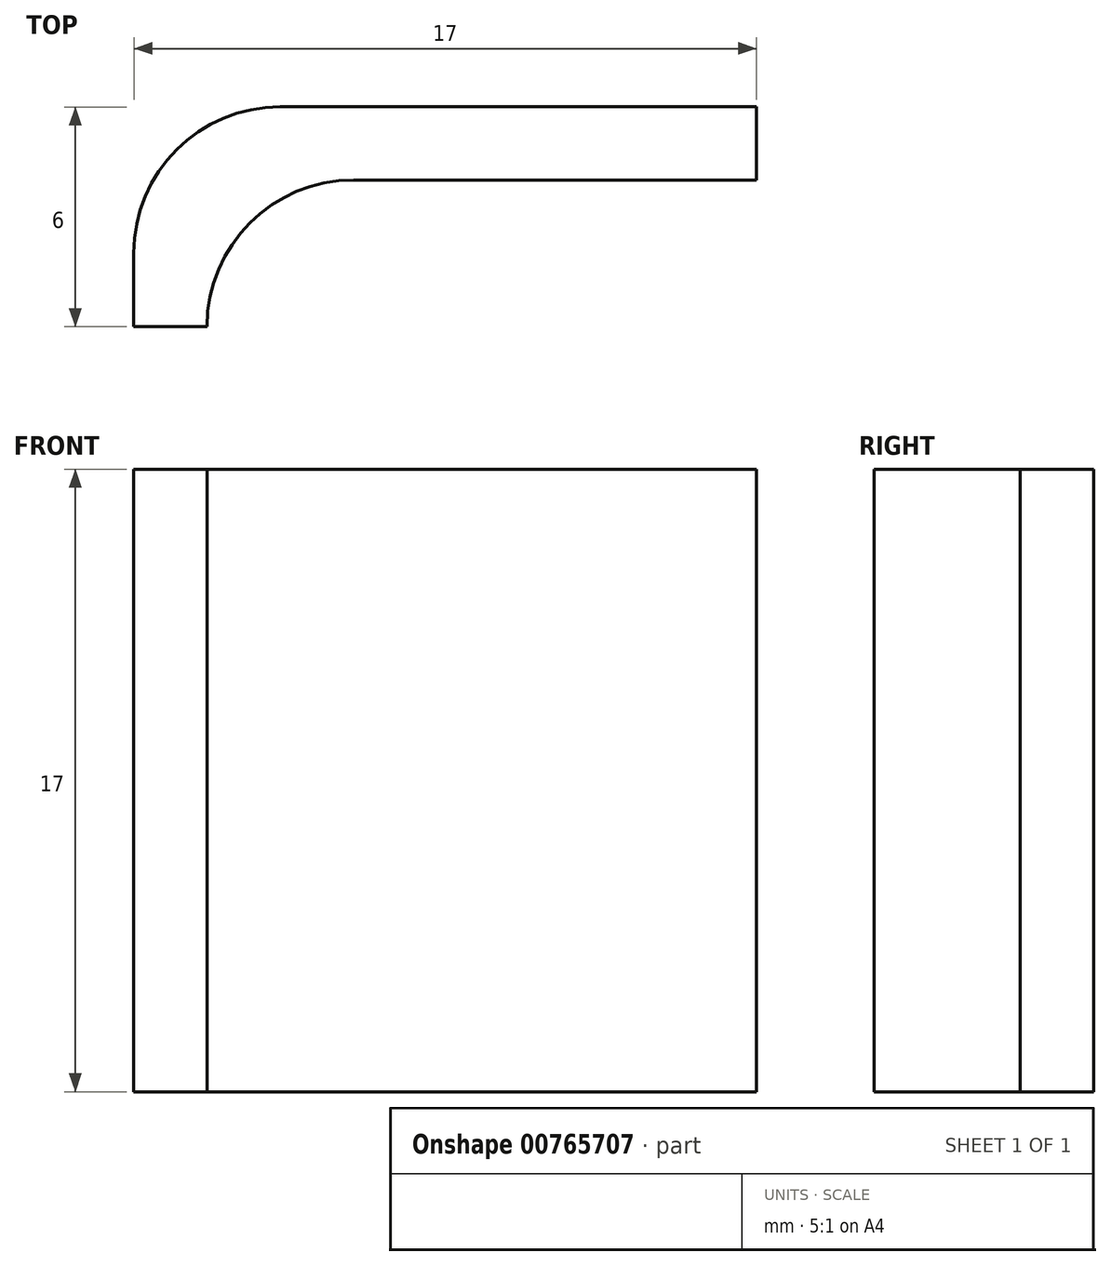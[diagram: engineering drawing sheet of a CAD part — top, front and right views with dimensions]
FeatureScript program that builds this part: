
annotation { "Feature Type Name" : "Feature", "Feature Type Description" : "" }
export const myFeature = defineFeature(function(context is Context, id is Id, definition is map)
    precondition{}
    {
        {
            var Q0;
            Q0=qCreatedBy(makeId("Top.planeOp"),FACE);
            var sketch = newSketch(context, id + "F0", { "sketchPlane" : qUnion([Q0])});
            skLineSegment(sketch, "E0", {"start": v(-18.7, 30.7) * mm, "end": v(-31.7, 30.7) * mm});
            skLineSegment(sketch, "E1", {"start": v(-35.7, 26.7) * mm, "end": v(-35.7, 24.7) * mm});
            skLineSegment(sketch, "E2", {"start": v(-18.7, 30.7) * mm, "end": v(-18.7, 28.7) * mm});
            skLineSegment(sketch, "E3", {"start": v(-18.7, 28.7) * mm, "end": v(-29.7, 28.7) * mm});
            skLineSegment(sketch, "E4", {"start": v(-35.7, 24.7) * mm, "end": v(-33.7, 24.7) * mm});
            skLineSegment(sketch, "E5", {"start": v(-33.7, 24.7) * mm, "end": v(-33.7, 24.7) * mm});
            skPoint(sketch, "E6.visualSharp", {"position": v(-35.7, 30.7) * mm});
            skArc(sketch, "E6.filletArc", {"start": v(-31.7, 30.7) * mm, "mid": v(-34.52, 29.52) * mm, "end": v(-35.7, 26.7) * mm});
            skPoint(sketch, "E7.visualSharp", {"position": v(-33.7, 28.7) * mm});
            skArc(sketch, "E7.filletArc", {"start": v(-29.7, 28.7) * mm, "mid": v(-32.52, 27.52) * mm, "end": v(-33.7, 24.7) * mm});
            skSolve(sketch);
        }
        {
            var Q0;
            Q0=makeQuery(id+"F0.imprint","IMPRINT",FACE,{"disambiguationData":[TD([[makeQuery(id+"F0.imprint","IMPRINT",EDGE,{"derivedFrom":sQuery(id+"F0.wireOp",EDGE,"E0")}),1.0]])]});
            extrude(context, id + "F1", {"entities" : qUnion([Q0]), "depth" : 17 * mm, "offsetDistance" : 25 * mm});
        }
    });
